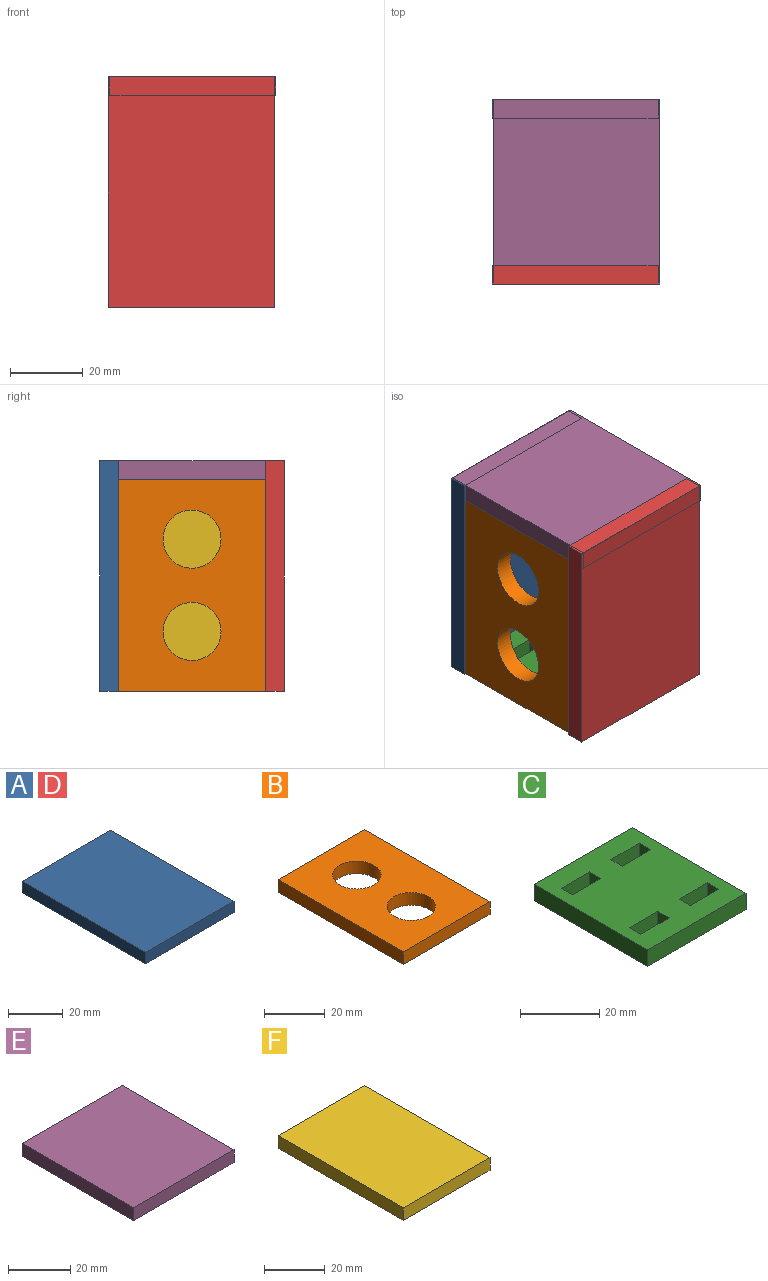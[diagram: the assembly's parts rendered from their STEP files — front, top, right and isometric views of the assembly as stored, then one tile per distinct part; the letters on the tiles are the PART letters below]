
ASSEMBLY  parts=6 mates=13
PART A: 6 faces, bbox 45.7x63.5x5.1 mm
  f0: plane 45.72x5.08mm, normal (0,1,0), area 232.3mm2, adj f1,f3,f4,f5
  f1: plane 63.5x5.08mm, normal (-1,0,0), area 322.6mm2, adj f0,f2,f4,f5
  f2: plane 45.72x5.08mm, normal (0,-1,0), area 232.3mm2, adj f1,f3,f4,f5
  f3: plane 63.5x5.08mm, normal (1,0,0), area 322.6mm2, adj f0,f2,f4,f5
  f4: plane 63.5x45.72mm, normal (0,0,1), area 2903.2mm2, adj f0,f1,f2,f3
  f5: plane 63.5x45.72mm, normal (0,0,-1), area 2903.2mm2, adj f0,f1,f2,f3
PART B: 8 faces, bbox 40.6x58.4x5.1 mm
  f0: plane 40.64x5.08mm, normal (0,1,0), area 206.5mm2, adj f1,f3,f4,f5
  f1: plane 58.42x5.08mm, normal (-1,0,0), area 296.8mm2, adj f0,f2,f4,f5
  f2: plane 40.64x5.08mm, normal (0,-1,0), area 206.5mm2, adj f1,f3,f4,f5
  f3: plane 58.42x5.08mm, normal (1,0,0), area 296.8mm2, adj f0,f2,f4,f5
  f4: plane 58.42x40.64mm, normal (0,0,1), area 1972mm2, adj f0,f1,f2,f3,f6,f7
  f5: plane 58.42x40.64mm, normal (0,0,-1), area 1972mm2, adj f0,f1,f2,f3,f6,f7
  f6: cylinder r=8mm len=16mm, axis (0,0,1), area 255.4mm2, adj f4,f5
  f7: cylinder r=8mm len=16mm, axis (0,0,1), area 255.4mm2, adj f4,f5
PART C: 22 faces, bbox 35.1x40.6x5.1 mm
  f0: plane 40.64x35.05mm, normal (0,0,1), area 1259.4mm2, adj f2,f3,f4,f5,f6,f7,f8,f9
  f1: plane 40.64x35.05mm, normal (0,0,-1), area 1259.4mm2, adj f2,f3,f4,f5,f6,f7,f8,f9
  f2: plane 35.05x5.08mm, normal (0,1,0), area 178.1mm2, adj f0,f1,f3,f5
  f3: plane 40.64x5.08mm, normal (-1,0,0), area 206.5mm2, adj f0,f1,f2,f4
  f4: plane 35.05x5.08mm, normal (0,-1,0), area 178.1mm2, adj f0,f1,f3,f5
  f5: plane 40.64x5.08mm, normal (1,0,0), area 206.5mm2, adj f0,f1,f2,f4
  f6: plane 10.16x5.08mm, normal (0,-1,0), area 51.6mm2, adj f0,f1,f7,f9
  f7: plane 5.08x4.06mm, normal (1,0,0), area 20.6mm2, adj f0,f1,f6,f8
  f8: plane 10.16x5.08mm, normal (0,1,0), area 51.6mm2, adj f0,f1,f7,f9
  f9: plane 5.08x4.06mm, normal (-1,0,0), area 20.6mm2, adj f0,f1,f6,f8
  f10: plane 10.16x5.08mm, normal (0,-1,0), area 51.6mm2, adj f0,f1,f11,f13
  f11: plane 5.08x4.06mm, normal (1,0,0), area 20.6mm2, adj f0,f1,f10,f12
  f12: plane 10.16x5.08mm, normal (0,1,0), area 51.6mm2, adj f0,f1,f11,f13
  f13: plane 5.08x4.06mm, normal (-1,0,0), area 20.6mm2, adj f0,f1,f10,f12
  f14: plane 5.08x4.06mm, normal (1,0,0), area 20.6mm2, adj f0,f1,f15,f17
  f15: plane 10.16x5.08mm, normal (0,1,0), area 51.6mm2, adj f0,f1,f14,f16
  f16: plane 5.08x4.06mm, normal (-1,0,0), area 20.6mm2, adj f0,f1,f15,f17
  f17: plane 10.16x5.08mm, normal (0,-1,0), area 51.6mm2, adj f0,f1,f14,f16
  f18: plane 5.08x4.06mm, normal (1,0,0), area 20.6mm2, adj f0,f1,f19,f21
  f19: plane 10.16x5.08mm, normal (0,1,0), area 51.6mm2, adj f0,f1,f18,f20
  f20: plane 5.08x4.06mm, normal (-1,0,0), area 20.6mm2, adj f0,f1,f19,f21
  f21: plane 10.16x5.08mm, normal (0,-1,0), area 51.6mm2, adj f0,f1,f18,f20
PART D: same geometry as A
PART E: 6 faces, bbox 45.7x50.8x5.1 mm
  f0: plane 45.72x5.08mm, normal (0,1,0), area 232.3mm2, adj f1,f3,f4,f5
  f1: plane 50.8x5.08mm, normal (-1,0,0), area 258.1mm2, adj f0,f2,f4,f5
  f2: plane 45.72x5.08mm, normal (0,-1,0), area 232.3mm2, adj f1,f3,f4,f5
  f3: plane 50.8x5.08mm, normal (1,0,0), area 258.1mm2, adj f0,f2,f4,f5
  f4: plane 50.8x45.72mm, normal (0,0,1), area 2322.6mm2, adj f0,f1,f2,f3
  f5: plane 50.8x45.72mm, normal (0,0,-1), area 2322.6mm2, adj f0,f1,f2,f3
PART F: 6 faces, bbox 40.6x58.4x5.1 mm
  f0: plane 40.64x5.08mm, normal (0,1,0), area 206.5mm2, adj f1,f3,f4,f5
  f1: plane 58.42x5.08mm, normal (-1,0,0), area 296.8mm2, adj f0,f2,f4,f5
  f2: plane 40.64x5.08mm, normal (0,-1,0), area 206.5mm2, adj f1,f3,f4,f5
  f3: plane 58.42x5.08mm, normal (1,0,0), area 296.8mm2, adj f0,f2,f4,f5
  f4: plane 58.42x40.64mm, normal (0,0,1), area 2374.2mm2, adj f0,f1,f2,f3
  f5: plane 58.42x40.64mm, normal (0,0,-1), area 2374.2mm2, adj f0,f1,f2,f3
PLACE A rot(axis=(-1,0,0),90deg) t=(-16.41,6.05,44.75)mm
PLACE B rot(axis=(0.58,-0.58,-0.58),120deg) t=(-47.87,-31.01,38.43)mm
PLACE C t=(-10.82,-6,9.84)mm
PLACE D rot(axis=(1,0,0),90deg) t=(-16.41,-34.59,38.43)mm
PLACE E rot(axis=(-0.08,1,-0.01),0deg) t=(-15.9,-11.08,68.26)mm
PLACE F rot(axis=(0.58,0.58,0.58),120deg) t=(-12.82,2.46,38.43)mm
MATE planar A.f0 <-> C.f1  axis (0,0,-1) through (-30.6,8.59,9.84)mm
MATE planar E.f2 <-> D.f4  axis (0,-1,0) through (-30.09,-39.67,70.8)mm
MATE planar E.f5 <-> F.f0  axis (0,0,-1) through (-30.09,-14.27,68.26)mm
MATE planar A.f3 <-> F.f4  axis (1,0,0) through (-7.74,8.59,41.59)mm
MATE planar D.f2 <-> C.f1  axis (0,0,-1) through (-30.6,-37.13,9.84)mm
MATE planar D.f3 <-> F.f4  axis (1,0,0) through (-7.74,-37.13,41.59)mm
MATE planar F.f5 <-> C.f5  axis (-1,0,0) through (-12.82,-14.27,39.05)mm
MATE planar A.f5 <-> F.f3  axis (0,-1,0) through (-30.6,6.05,41.59)mm
MATE planar E.f1 <-> B.f4  axis (-1,0,0) through (-52.95,-14.27,70.8)mm
MATE planar B.f2 <-> C.f1  axis (0,0,-1) through (-50.41,-14.27,9.84)mm
MATE planar B.f5 <-> C.f3  axis (1,0,0) through (-47.87,-14.27,39.05)mm
MATE planar F.f2 <-> C.f1  axis (0,0,-1) through (-10.28,-14.27,9.84)mm
MATE planar D.f5 <-> F.f1  axis (0,1,0) through (-30.6,-34.59,41.59)mm
